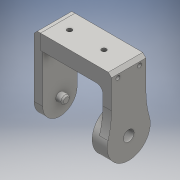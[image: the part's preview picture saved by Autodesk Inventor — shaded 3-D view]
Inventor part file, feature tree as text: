
AUTODESK INVENTOR PART (.ipt)
format: ipt  version: 2016 (Build 200138000, 138)  size: 287,744 bytes
history: native  units: mm
features: sketch x14, extrude x12, hole x5, chamfer x3, fillet x2
ambient origin geometry x8: Origin, YZ Plane, XZ Plane, XY Plane, X Axis, Y Axis, Z Axis, Center Point
bodies: Solid1 (feature_tree), Solid2 (feature_tree)
feature tree (36):
  extrude  "Extrusion1"  Depth=4.0mm
  extrude  "Extrusion2"  Depth=16.0mm
  extrude  "Extrusion3"  Depth=7.0mm
  extrude  "Extrusion4"  Depth=2.5mm
  chamfer  "Chamfer1"  Distance=40.0mm Angle=360.0deg
  extrude  "Extrusion5"  Depth=0.6mm TaperAngle=45.0deg
  extrude  "Extrusion6"  Depth=3.0mm TaperAngle=0.0deg
  hole  "Hole1"  [1 undecoded]
  extrude  "Extrusion7"  Depth=3.0mm TaperAngle=0.0deg
  extrude  "Extrusion8"  Depth=4.0mm TaperAngle=0.0deg
  extrude  "Extrusion9"  Depth=10.0mm
  extrude  "Extrusion10"  Depth=10.0mm
  hole  "Hole2"  [1 undecoded]
  hole  "Hole3"  [1 undecoded]
  extrude  "Extrusion11"  Depth=3.0mm
  chamfer  "Chamfer2"  Distance=1.5mm Angle=45.0deg
  fillet  "Fillet1"  Radius=40.0mm
  chamfer  "Chamfer3"  Distance=16.0mm
  fillet  "Fillet2"  Radius=4.2mm
  hole  "Hole4"  [1 undecoded]
  extrude  "Extrusion12"  Depth=2.5mm TaperAngle=0.0deg
  hole  "Hole5"  [1 undecoded]
  sketch  "Sketch1"  dims[d1=4.0mm d2=4.0mm]
  sketch  "Sketch2"  dims[d3=16.0mm d4=0.0mm d5=20.0mm]
  sketch  "Sketch3"  dims[d6=7.0mm d7=0.0mm d8=17.65mm]
  sketch  "Sketch4"  dims[d9=2.5mm d10=0.0mm d11=3.9mm]
  sketch  "Sketch5"  dims[d12=6.0mm d13=40.0mm d15=360.0deg]
  sketch  "Sketch6"  dims[d17=3.0mm d18=0.0mm d19=0.6mm d20=2.0mm d21=45.0deg]
  sketch  "Sketch7"  dims[d22=3.0mm d23=0.0mm d24=3.0mm d25=0.0mm]
  sketch  "Sketch8"  dims[d26=10.0mm d27=5.0mm]
  sketch  "Sketch9"  dims[d28=1.9mm d29=6.0mm d30=4.0mm d31=2.0mm d32=90.0deg d33=8.0mm d34=20.594885mm d35=3.0mm d36=0.0mm]
  sketch  "Sketch10"  dims[d37=22.0mm d38=0.0mm d39=4.0mm d40=0.0mm]
  sketch  "Sketch11"  dims[d41=1.0mm d42=0.0mm d43=10.0mm d44=10.0mm]
  sketch  "Sketch12"  dims[d45=2.1mm d46=6.0mm d47=4.0mm d48=2.0mm d49=90.0deg d50=8.0mm d51=20.594885mm d52=10.0mm d53=10.0mm]
  sketch  "Sketch13"  dims[d54=2.1mm d55=6.0mm d56=4.0mm d57=2.0mm d58=90.0deg d59=8.0mm d60=20.594885mm d61=3.8mm]
  sketch  "Sketch14"  dims[d62=3.0mm d63=0.0mm d64=0.6mm d65=2.0mm d66=45.0deg d67=3.0mm d68=1.5mm d69=2.0mm d70=45.0deg d71=40.0mm d72=16.0mm d73=2.2mm d74=6.0mm d75=4.0mm d76=2.0mm d77=90.0deg d78=8.0mm d79=20.594885mm d80=4.2mm d81=4.2mm d82=2.5mm d83=0.0mm d84=10.0mm d85=10.0mm d86=5.0mm d87=6.0mm d88=4.0mm d89=2.0mm d90=90.0deg d91=8.0mm d92=20.594885mm]
note: 5 required parameter values undecoded (feature->parameter linkage not recoverable at this tier; creation-order binding heuristic only, values carry confidence <= 0.55)
